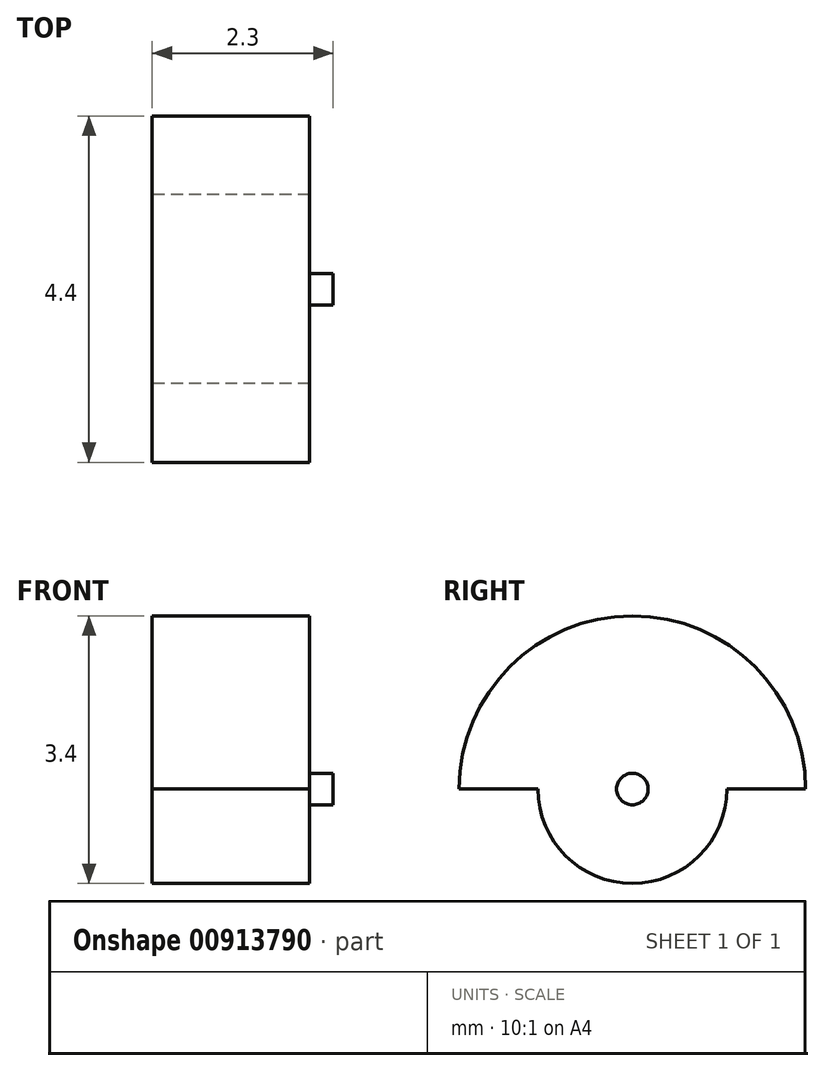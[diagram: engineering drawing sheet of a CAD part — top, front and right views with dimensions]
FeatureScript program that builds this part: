
annotation { "Feature Type Name" : "Feature", "Feature Type Description" : "" }
export const myFeature = defineFeature(function(context is Context, id is Id, definition is map)
    precondition{}
    {
        {
            var Q0;
            Q0=qCreatedBy(makeId("Right.planeOp"),FACE);
            var sketch = newSketch(context, id + "F0", { "sketchPlane" : qUnion([Q0])});
            skArc(sketch, "E0", {"start": v(-2.2, 0) * mm, "mid": v(0, 2.2) * mm, "end": v(2.2, 0) * mm});
            skArc(sketch, "E1", {"start": v(-1.2, 0) * mm, "mid": v(0, -1.2) * mm, "end": v(1.2, 0) * mm});
            skLineSegment(sketch, "E2", {"start": v(-2.2, 0) * mm, "end": v(-1.2, 0) * mm});
            skLineSegment(sketch, "E3", {"start": v(1.2, 0) * mm, "end": v(2.2, 0) * mm});
            skSolve(sketch);
        }
        {
            var Q0;
            Q0 = qSketchRegion(id + "F0", true);
            extrude(context, id + "F1", {"entities" : qUnion([Q0]), "depth" : 2 * mm, "offsetDistance" : 25.4 * mm});
        }
        {
            var Q0;
            Q0=makeQuery(id+"F1.opExtrude","CAP_FACE",FACE,{"disambiguationData":[OSD([sQuery(id+"F0.wireOp",EDGE,"E0"),sQuery(id+"F0.wireOp",EDGE,"E1"),sQuery(id+"F0.wireOp",EDGE,"E2"),sQuery(id+"F0.wireOp",EDGE,"E3")])],"isStart":false});
            var sketch = newSketch(context, id + "F2", { "sketchPlane" : qUnion([Q0])});
            skCircle(sketch, "E4", {"center": v(0, 0) * mm, "radius": 0.2 * mm});
            skSolve(sketch);
        }
        {
            var Q0;
            Q0 = qSketchRegion(id + "F2", true);
            extrude(context, id + "F3", {"entities" : qUnion([Q0]), "operationType" : NewBodyOperationType.ADD, "depth" : 0.3 * mm, "offsetDistance" : 25.4 * mm});
        }
    });
